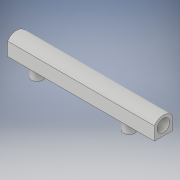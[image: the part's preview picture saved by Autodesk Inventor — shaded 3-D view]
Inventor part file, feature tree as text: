
AUTODESK INVENTOR PART (.ipt)
format: ipt  version: 2018.3 (Build 223284000, 284)  size: 147,456 bytes
history: native  units: in
note: dims shown in document units (in); Inventor stores cm internally (conversion verified against a paired STEP export)
features: sketch x4, extrude x3, plane x3, hole x2, fillet x1
ambient origin geometry x8: Origin, YZ Plane, XZ Plane, XY Plane, X Axis, Y Axis, Z Axis, Center Point
bodies: Solid1 (feature_tree)
feature tree (13):
  extrude  "Extrusion1"  Depth=0.158in
  plane  "Work Plane1"
  sketch  "Sketch2"  dims[d2=0.158in d3=0.0in d4=0.0in]
  hole  "Hole1"  [1 undecoded]
  extrude  "Extrusion2"  Depth=1.1in
  plane  "Work Plane2"
  sketch  "Sketch3"  dims[d5=0.091in d6=0.75in d7=0.109in d8=1.1in d9=0.5635in d10=1.0in d11=0.8108in d12=0.19in]
  extrude  "Extrusion3"  TaperAngle=0.0deg  [1 undecoded]
  plane  "Work Plane3"
  hole  "Hole2"  [1 undecoded]
  fillet  "Fillet1"  Radius=0.098in
  sketch  "Sketch1"  dims[d0=1.28in d1=0.158in]
  sketch  "Sketch4"  dims[d13=1.408in d14=0.0in d15=0.0in d16=0.098in d17=0.098in d18=0.18in d19=0.8016in d20=0.104in d21=0.0in d22=0.0in d23=0.05in d24=0.75in d25=0.109in d26=1.1in d27=0.5635in d28=0.06in d29=0.8108in d30=0.015in]
note: 3 required parameter values undecoded (feature->parameter linkage not recoverable at this tier; creation-order binding heuristic only, values carry confidence <= 0.55)
